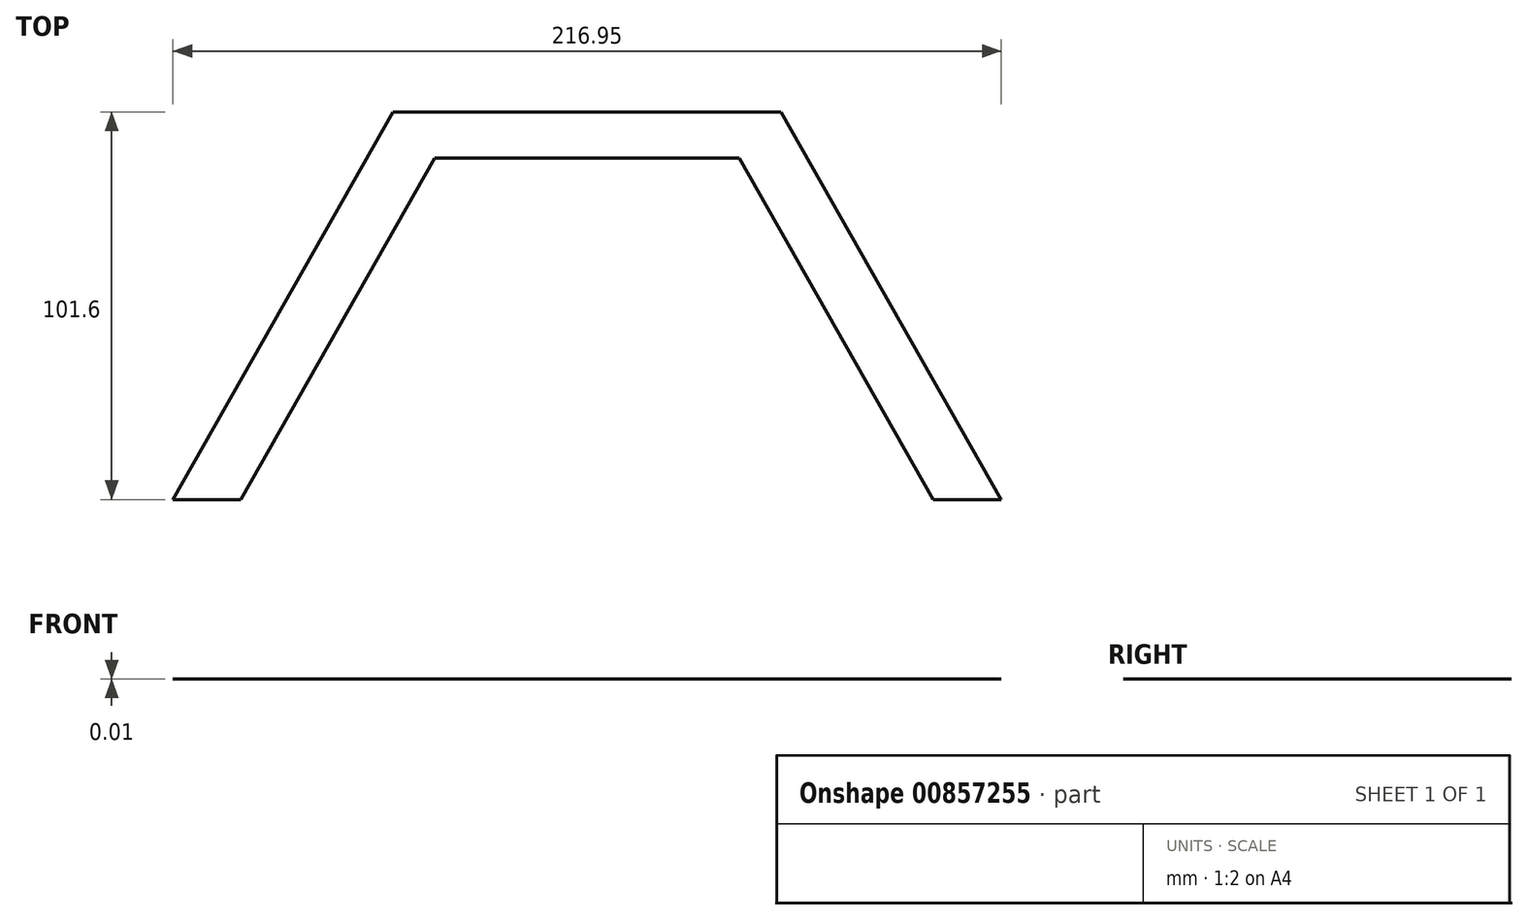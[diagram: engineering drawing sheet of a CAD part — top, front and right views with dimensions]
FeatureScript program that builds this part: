
annotation { "Feature Type Name" : "Feature", "Feature Type Description" : "" }
export const myFeature = defineFeature(function(context is Context, id is Id, definition is map)
    precondition{}
    {
        {
            var Q0;
            Q0=qCreatedBy(makeId("Top.planeOp"),FACE);
            var sketch = newSketch(context, id + "F0", { "sketchPlane" : qUnion([Q0])});
            skLineSegment(sketch, "E0.bottom", {"start": v(-6.46, 56.66) * mm, "end": v(-57.26, 56.66) * mm});
            skLineSegment(sketch, "E0.top", {"start": v(-97.12, -44.94) * mm, "end": v(-114.93, -44.94) * mm});
            skLineSegment(sketch, "E1", {"start": v(-57.26, 56.66) * mm, "end": v(-114.93, -44.94) * mm});
            skLineSegment(sketch, "E2.MirrorCS", {"start": v(-6.46, 56.66) * mm, "end": v(44.34, 56.66) * mm});
            skLineSegment(sketch, "E3.MirrorCS", {"start": v(44.34, 56.66) * mm, "end": v(102.02, -44.94) * mm});
            skLineSegment(sketch, "E4.MirrorCS", {"start": v(84.2, -44.94) * mm, "end": v(102.02, -44.94) * mm});
            skLineSegment(sketch, "E5", {"start": v(-97.12, -44.94) * mm, "end": v(-46.31, 44.57) * mm});
            skLineSegment(sketch, "E6", {"start": v(-46.31, 44.57) * mm, "end": v(-6.46, 44.57) * mm});
            skLineSegment(sketch, "E7.MirrorCS", {"start": v(33.4, 44.57) * mm, "end": v(-6.46, 44.57) * mm});
            skLineSegment(sketch, "E8.MirrorCS", {"start": v(84.2, -44.94) * mm, "end": v(33.4, 44.57) * mm});
            skSolve(sketch);
        }
        {
            var Q0;
            Q0=makeQuery(id+"F0.imprint","IMPRINT",FACE,{"disambiguationData":[TD([[makeQuery(id+"F0.imprint","IMPRINT",EDGE,{"derivedFrom":sQuery(id+"F0.wireOp",EDGE,"E0.left")}),1.0]])]});
            var Q1;
            Q1=makeQuery(id+"F0.imprint","IMPRINT",FACE,{"disambiguationData":[TD([[makeQuery(id+"F0.imprint","IMPRINT",EDGE,{"derivedFrom":sQuery(id+"F0.wireOp",EDGE,"E0.bottom")}),1.0]])]});
            extrude(context, id + "F1", {"entities" : qUnion([Q0, Q1]), "depth" : 3 / 203.2 * mm, "offsetDistance" : 25 * mm});
        }
    });
